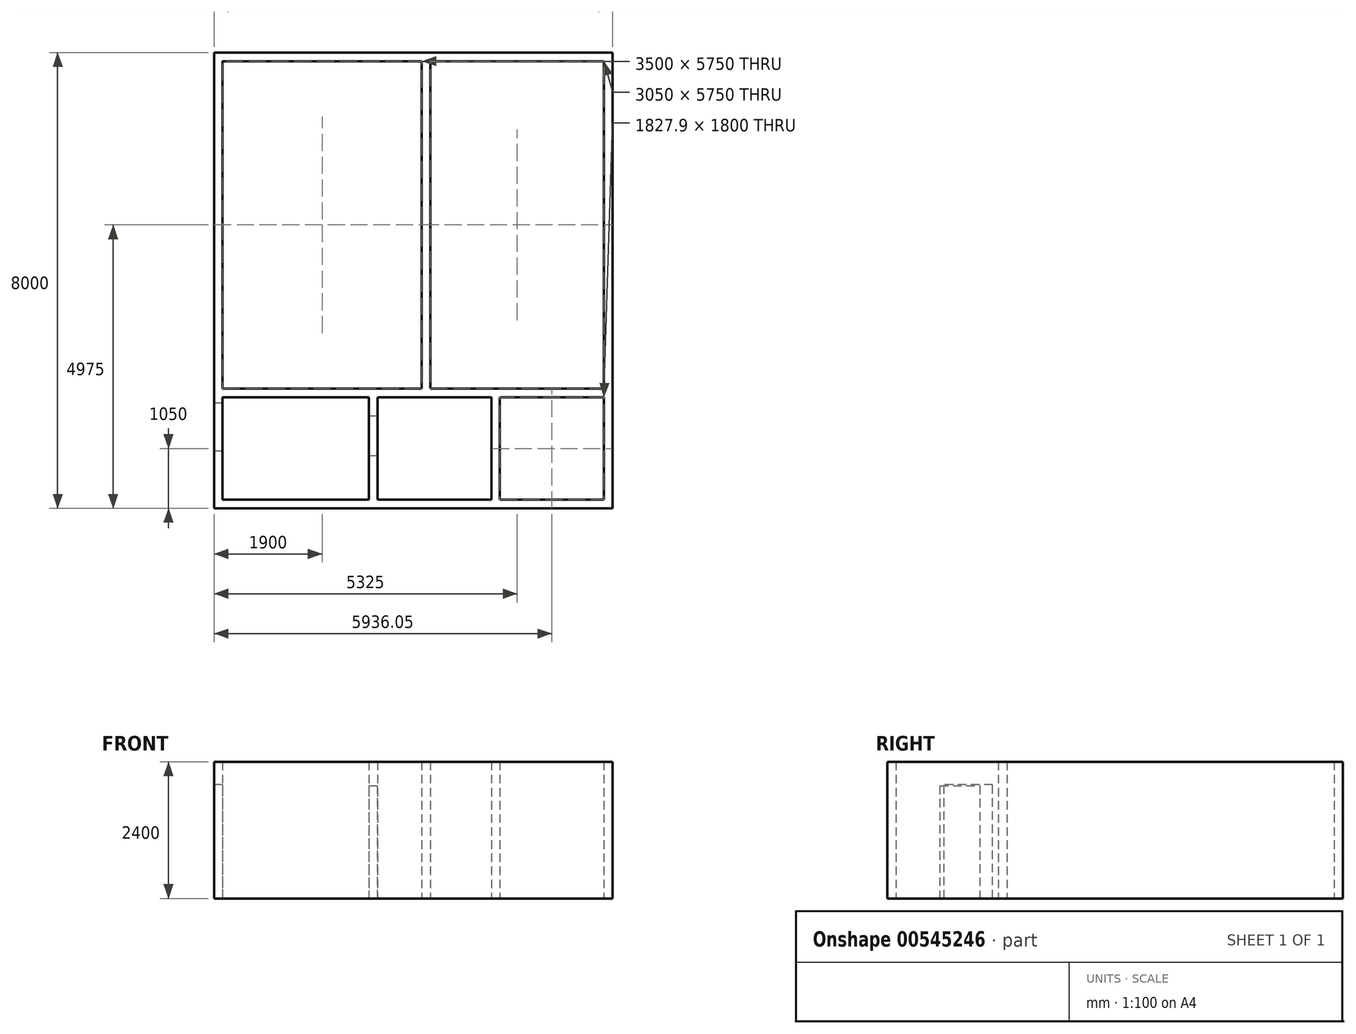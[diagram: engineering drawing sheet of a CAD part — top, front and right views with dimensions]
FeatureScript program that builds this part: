
annotation { "Feature Type Name" : "Feature", "Feature Type Description" : "" }
export const myFeature = defineFeature(function(context is Context, id is Id, definition is map)
    precondition{}
    {
        {
            var Q0;
            Q0=qCreatedBy(makeId("Top.planeOp"),FACE);
            var sketch = newSketch(context, id + "F0", { "sketchPlane" : qUnion([Q0])});
            skLineSegment(sketch, "E0.bottom", {"start": v(3500, -4000) * mm, "end": v(-3500, -4000) * mm});
            skLineSegment(sketch, "E0.top", {"start": v(3500, 4000) * mm, "end": v(-3500, 4000) * mm});
            skLineSegment(sketch, "E0.left", {"start": v(3500, -4000) * mm, "end": v(3500, 4000) * mm});
            skLineSegment(sketch, "E0.right", {"start": v(-3500, -4000) * mm, "end": v(-3500, 4000) * mm});
            skPoint(sketch, "E0.middle", {"position": v(0, 0) * mm});
            skLineSegment(sketch, "E1.0", {"start": v(-3350, -3850) * mm, "end": v(-3350, -2050) * mm});
            skLineSegment(sketch, "E1.1", {"start": v(3350, -3850) * mm, "end": v(-3350, -3850) * mm});
            skLineSegment(sketch, "E1.2", {"start": v(3350, -3850) * mm, "end": v(3350, -2050) * mm});
            skLineSegment(sketch, "E1.3", {"start": v(3350, 3850) * mm, "end": v(300, 3850) * mm});
            skLineSegment(sketch, "E2", {"start": v(-3350, -2050) * mm, "end": v(-777.9, -2050) * mm});
            skLineSegment(sketch, "E3", {"start": v(-627.9, -2050) * mm, "end": v(-627.9, -3850) * mm});
            skLineSegment(sketch, "E4", {"start": v(-627.9, -2050) * mm, "end": v(1372.1, -2050) * mm});
            skLineSegment(sketch, "E5", {"start": v(1372.1, -2050) * mm, "end": v(1372.1, -3850) * mm});
            skLineSegment(sketch, "E6.0", {"start": v(-777.9, -2050) * mm, "end": v(-777.9, -3850) * mm});
            skLineSegment(sketch, "E7.0", {"start": v(1522.1, -2050) * mm, "end": v(1522.1, -3850) * mm});
            skLineSegment(sketch, "E8.trimOffspring", {"start": v(1522.1, -2050) * mm, "end": v(3350, -2050) * mm});
            skLineSegment(sketch, "E9", {"start": v(-3350, -1900) * mm, "end": v(150, -1900) * mm});
            skLineSegment(sketch, "E10.trimOffspring", {"start": v(3350, -1900) * mm, "end": v(3350, 3850) * mm});
            skLineSegment(sketch, "E11.trimOffspring", {"start": v(-3350, -1900) * mm, "end": v(-3350, 3850) * mm});
            skLineSegment(sketch, "E12", {"start": v(150, 3850) * mm, "end": v(150, -1900) * mm});
            skLineSegment(sketch, "E13.0", {"start": v(300, 3850) * mm, "end": v(300, -1900) * mm});
            skLineSegment(sketch, "E14.trimOffspring", {"start": v(300, -1900) * mm, "end": v(3350, -1900) * mm});
            skLineSegment(sketch, "E15.trimOffspring", {"start": v(150, 3850) * mm, "end": v(-3350, 3850) * mm});
            skSolve(sketch);
        }
        {
            var Q0;
            Q0 = qSketchRegion(id + "F0", true);
            extrude(context, id + "F1", {"entities" : qUnion([Q0]), "depth" : 2400 * mm, "offsetDistance" : 25 * mm});
        }
        {
            var Q0;
            Q0=makeQuery(id+"F1.opExtrude","SWEPT_FACE",FACE,{"disambiguationData":[OSD([sQuery(id+"F0.wireOp",EDGE,"E0.right")])]});
            var sketch = newSketch(context, id + "F2", { "sketchPlane" : qUnion([Q0])});
            skLineSegment(sketch, "E16.bottom", {"start": v(2150, 0) * mm, "end": v(3000, 0) * mm});
            skLineSegment(sketch, "E16.top", {"start": v(2150, 2000) * mm, "end": v(3000, 2000) * mm});
            skLineSegment(sketch, "E16.left", {"start": v(2150, 0) * mm, "end": v(2150, 2000) * mm});
            skLineSegment(sketch, "E16.right", {"start": v(3000, 0) * mm, "end": v(3000, 2000) * mm});
            skSolve(sketch);
        }
        {
            var Q0;
            Q0=makeQuery(id+"F2.imprint","IMPRINT",FACE,{"disambiguationData":[TD([[makeQuery(id+"F2.imprint","IMPRINT",EDGE,{"derivedFrom":sQuery(id+"F2.wireOp",EDGE,"E16.bottom")}),-1.0]])]});
            extrude(context, id + "F3", {"entities" : qUnion([Q0]), "operationType" : NewBodyOperationType.REMOVE, "endBound" : BoundingType.UP_TO_NEXT, "oppositeDirection" : true, "depth" : 25 * mm, "offsetDistance" : 25 * mm});
        }
        {
            var Q0;
            Q0=makeQuery(id+"F1.opExtrude","SWEPT_FACE",FACE,{"disambiguationData":[OSD([sQuery(id+"F0.wireOp",EDGE,"E3")])]});
            var sketch = newSketch(context, id + "F4", { "sketchPlane" : qUnion([Q0])});
            skLineSegment(sketch, "E17.bottom", {"start": v(-2376.2, 0) * mm, "end": v(-3076.2, 0) * mm});
            skLineSegment(sketch, "E17.top", {"start": v(-2376.2, 1978.06) * mm, "end": v(-3076.2, 1978.06) * mm});
            skLineSegment(sketch, "E17.left", {"start": v(-2376.2, 0) * mm, "end": v(-2376.2, 1978.06) * mm});
            skLineSegment(sketch, "E17.right", {"start": v(-3076.2, 0) * mm, "end": v(-3076.2, 1978.06) * mm});
            skSolve(sketch);
        }
        {
            var Q0;
            Q0=makeQuery(id+"F4.imprint","IMPRINT",FACE,{"disambiguationData":[TD([[makeQuery(id+"F4.imprint","IMPRINT",EDGE,{"derivedFrom":sQuery(id+"F4.wireOp",EDGE,"E17.bottom")}),-1.0]])]});
            extrude(context, id + "F5", {"entities" : qUnion([Q0]), "operationType" : NewBodyOperationType.REMOVE, "endBound" : BoundingType.UP_TO_NEXT, "oppositeDirection" : true, "depth" : 25 * mm, "offsetDistance" : 25 * mm});
        }
    });
